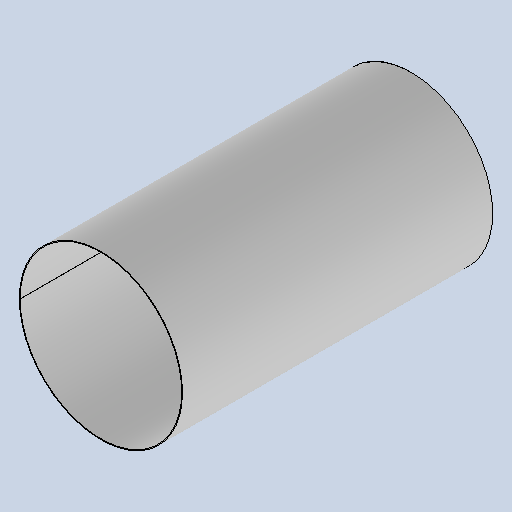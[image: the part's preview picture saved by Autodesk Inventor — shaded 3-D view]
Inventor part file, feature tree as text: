
AUTODESK INVENTOR PART (.ipt)
format: ipt  version: 2025 (Build 290162010, 162A)  size: 133,632 bytes
history: native  units: mm
features: other x2, revolve x1, sketch x1
ambient origin geometry x8: Origin, YZ Plane, XZ Plane, XY Plane, X Axis, Y Axis, Z Axis, Center Point
bodies: Solid1 (feature_tree)
feature tree (4):
  revolve  "Revolution1"  [1 undecoded]
  other  "A-Side Definition"
  sketch  "Sketch1"  dims[d0=320.0mm d1=0.8mm d2=168.3mm d3=62.8144mm]
  other  "Definition1"
note: 1 required parameter value undecoded (feature->parameter linkage not recoverable at this tier; creation-order binding heuristic only, values carry confidence <= 0.55)
